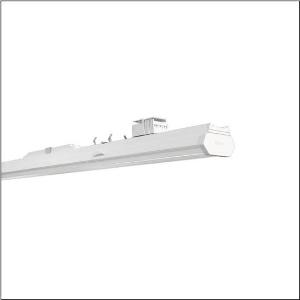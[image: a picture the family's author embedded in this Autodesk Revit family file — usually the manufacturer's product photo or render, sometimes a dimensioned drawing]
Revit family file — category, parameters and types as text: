
# Revit family: licross_r__11_protected_mo_51tp12cn58xf_fcc9
name_source: partatom
category: Lighting Fixtures
units: mm (PartAtom-declared; Revit-internal decimal feet)

## family parameters
Cut with Voids When Loaded = No
Host = Face
Light Source = No
Part Type = Normal
Room Calculation Point = No
Round Connector Dimension = Use Diameter
Shared = No

## types (1)
- --- (1 x LED, 8190 lm, 49 W, 5000K)
    Apparent Load = 49 VA
    CIE Flux Codes = 73 92 98 99 100
    Color Rendering = 80
    Color Temperature = 5000K
    Default Elevation = 1800 mm
    Description = Licross® 11 Protected MO, luminaire insert, of sheet steel, galvanised, coil coated, white, length: 1.500mm, width: 90mm, height: 101mm, LED rated luminous flux: 8.190lm, light colour: 850, control gear: ON/OFF Multilumen, CLOi, control gear: ECG Multilumen, with plug, 3-pole, with phase selection, mains connection: 220..240V, AC, 50/60Hz, start of lifetime: 49W, end of service life: 54W, halogen-free wiring, primary optical cover: cover, of PMMA, light emission: direct distribution, primary light characteristic: symmetric, protection rating (complete): IP64, insulation class (complete): insulation class I (protective earthing), certification: CE, ENEC, VDE, UKCA, protection symbol: D if used in an environment with conductive dust loads with corresponding accessories, impact resistance: IK06, permissible ambient temperature for indoor applications: -35..+40°C, reducing of maximum allowable ambient temperature of 5°C with ceiling mounting, corresponds to IFS (International Featured Standards) requirements for safety and quality in the food industry, LABS conformity tested according to VDMA 24364:2018-05, packaging unit: 1 piece
    Height = 92 mm
    Lamp = 1 x LED
    Lamp Light Flux = 8190 lm
    Lamp Power = 49 W
    Lamp count = 1
    Length = 1500 mm
    Luminous efficacy = 167 lm/W
    Manufacturer = Siteco
    ModVariant = No
    Model = 51TP12CN58XF
    Mounting Place = Ceiling
    Mounting Type = Pendant
    Number of Poles = 1
    OnlyDefault = Yes
    Power Factor = 1
    Product Name = Licross® 11 Protected MO
    Product group = luminaire insert
    ProductGroupID = 901
    Protection Class = Protection class I
    Protection Degree = IP 64
    RLX_Detail_Level = 1
    RLX_Emergency_Light_Flux = 0 lm
    RLX_Emergency_Type = 0
    RLX_Emergency_Type_DB = No
    RlxData = <blob elided: 22013 chars, md5=0ea13557>
    Socket = socket
    Standby Power = 0 W
    System Light Flux = 8190 lm
    System Power = 49 W
    Type Comments = factory setting: luminous flux: 100 % | (A | C | E) | 111 mA
    Type Image = l_1256148.jpg
    URL = http://relux.com
    VarID = @adj_175763
    Voltage = 0 V
    Weight = 0.00 kg
    Width = 88 mm

## geometry (parser evidence)
native form markers: Blend x4, Sweep x10
no freeform markers — native parametric forms only
